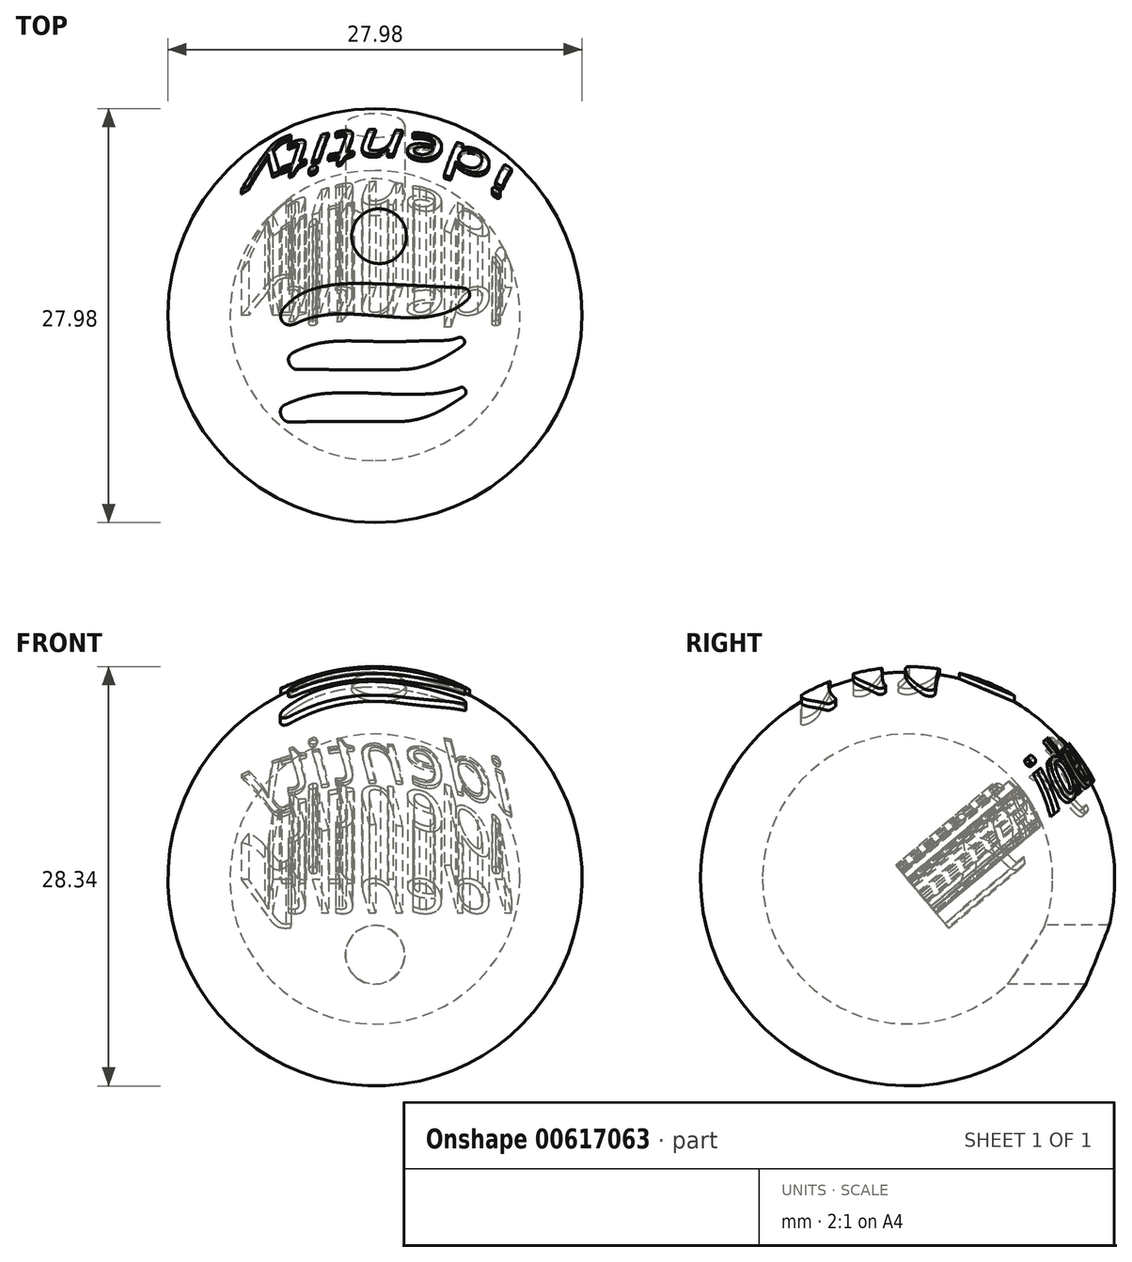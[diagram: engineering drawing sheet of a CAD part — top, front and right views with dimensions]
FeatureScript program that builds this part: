
annotation { "Feature Type Name" : "Feature", "Feature Type Description" : "" }
export const myFeature = defineFeature(function(context is Context, id is Id, definition is map)
    precondition{}
    {
        {
            var Q0;
            Q0=qCreatedBy(makeId("Top.planeOp"),FACE);
            var sketch = newSketch(context, id + "F0", { "sketchPlane" : qUnion([Q0])});
            skLineSegment(sketch, "E0", {"start": v(0, -10) * mm, "end": v(0, 10) * mm});
            skArc(sketch, "E1", {"start": v(0, 10) * mm, "mid": v(-10, 0) * mm, "end": v(0, -10) * mm});
            skSolve(sketch);
        }
        {
            var Q0;
            {var subQ0=sQuery(id+"F0.wireOp",EDGE,"E1");Q0=makeQuery(id+"F0.imprint","IMPRINT",FACE,{"disambiguationData":[TD([[makeQuery(id+"F0.imprint","IMPRINT",EDGE,{"derivedFrom":subQ0}),1.0]])]});}
            var Q1;
            Q1=sQuery(id+"F0.wireOp",EDGE,"E0");
            revolve(context, id + "F1", {"entities" : qUnion([Q0]), "axis" : qUnion([Q1]), "revolveType" : RevolveType.FULL});
        }
        {
            var Q0;
            Q0=makeQuery(id+"F1.opRevolve","SWEPT_BODY",BODY,{"disambiguationData":[OSD([sQuery(id+"F0.wireOp",EDGE,"E0"),sQuery(id+"F0.wireOp",EDGE,"E1")])]});
            var Q1;
            Q1=sQuery(id+"F0.wireOp",VERTEX,"NPe4G0ez-t7S9-9isL-QO5v-uuJu600mHcIT.center");
            var Q2;
            Q2=sQuery(id+"F0.wireOp",VERTEX,"E1.center");
            transform(context, id + "F2", {"entities" : qUnion([Q0]), "transformType" : TransformType.SCALE_UNIFORMLY, "scale" : 33.3, "scalePoint" : qUnion([Q2]), "makeCopy" : false});
        }
        {
            var Q0;
            Q0=qCreatedBy(makeId("Top.planeOp"),FACE);
            var sketch = newSketch(context, id + "F3", { "sketchPlane" : qUnion([Q0])});
            skArc(sketch, "E2", {"start": v(-4.66, 170.28) * mm, "mid": v(-7.58, 169.39) * mm, "end": v(-10.43, 168.3) * mm});
            skArc(sketch, "E3", {"start": v(-10.43, 168.3) * mm, "mid": v(-13.1, 167.06) * mm, "end": v(-15.68, 165.63) * mm});
            skArc(sketch, "E4", {"start": v(-15.68, 165.63) * mm, "mid": v(-18.2, 163.97) * mm, "end": v(-20.58, 162.14) * mm});
            skArc(sketch, "E5", {"start": v(-20.58, 162.14) * mm, "mid": v(-23, 160) * mm, "end": v(-25.3, 157.73) * mm});
            skArc(sketch, "E6", {"start": v(-25.3, 157.73) * mm, "mid": v(-31.47, 149.54) * mm, "end": v(-35.58, 140.15) * mm});
            skArc(sketch, "E7", {"start": v(-35.58, 140.15) * mm, "mid": v(-37.42, 130.07) * mm, "end": v(-36.87, 119.84) * mm});
            skArc(sketch, "E8", {"start": v(-36.87, 119.84) * mm, "mid": v(-33.98, 110.06) * mm, "end": v(-28.9, 101.23) * mm});
            skArc(sketch, "E9", {"start": v(-28.9, 101.23) * mm, "mid": v(-21.93, 93.88) * mm, "end": v(-13.42, 88.39) * mm});
            skArc(sketch, "E10", {"start": v(-13.42, 88.39) * mm, "mid": v(-4.52, 85.1) * mm, "end": v(4.86, 83.64) * mm});
            skArc(sketch, "E11", {"start": v(4.86, 83.64) * mm, "mid": v(14.1, 84.14) * mm, "end": v(23, 86.6) * mm});
            skArc(sketch, "E12", {"start": v(23, 86.6) * mm, "mid": v(31.14, 90.88) * mm, "end": v(38.15, 96.82) * mm});
            skArc(sketch, "E13", {"start": v(38.15, 96.82) * mm, "mid": v(43.87, 104.23) * mm, "end": v(47.95, 112.66) * mm});
            skArc(sketch, "E14", {"start": v(47.95, 112.66) * mm, "mid": v(48.9, 115.67) * mm, "end": v(49.58, 118.75) * mm});
            skArc(sketch, "E15", {"start": v(49.58, 118.75) * mm, "mid": v(50.08, 122.26) * mm, "end": v(50.36, 125.8) * mm});
            skArc(sketch, "E16", {"start": v(50.36, 125.8) * mm, "mid": v(50.43, 129.3) * mm, "end": v(50.27, 132.82) * mm});
            skArc(sketch, "E17", {"start": v(50.27, 132.82) * mm, "mid": v(49.9, 135.86) * mm, "end": v(49.24, 138.85) * mm});
            skArc(sketch, "E18", {"start": v(49.24, 138.85) * mm, "mid": v(46.19, 146.9) * mm, "end": v(41.61, 154.2) * mm});
            skArc(sketch, "E19", {"start": v(41.61, 154.2) * mm, "mid": v(35.64, 160.54) * mm, "end": v(28.58, 165.62) * mm});
            skArc(sketch, "E20", {"start": v(28.58, 165.62) * mm, "mid": v(20.7, 169.25) * mm, "end": v(12.28, 171.3) * mm});
            skArc(sketch, "E21", {"start": v(12.28, 171.3) * mm, "mid": v(3.76, 171.65) * mm, "end": v(-4.66, 170.28) * mm});
            skArc(sketch, "E22", {"start": v(-53.26, 50.77) * mm, "mid": v(-64.06, 49.8) * mm, "end": v(-74.8, 48.33) * mm});
            skArc(sketch, "E23", {"start": v(-74.8, 48.33) * mm, "mid": v(-84.6, 46.48) * mm, "end": v(-94.27, 44.06) * mm});
            skArc(sketch, "E24", {"start": v(-94.27, 44.06) * mm, "mid": v(-102.95, 41.3) * mm, "end": v(-111.44, 38.01) * mm});
            skArc(sketch, "E25", {"start": v(-111.44, 38.01) * mm, "mid": v(-118.91, 34.44) * mm, "end": v(-126.06, 30.25) * mm});
            skArc(sketch, "E26", {"start": v(-126.06, 30.25) * mm, "mid": v(-129.48, 27.88) * mm, "end": v(-132.74, 25.3) * mm});
            skArc(sketch, "E27", {"start": v(-132.74, 25.3) * mm, "mid": v(-136.56, 21.93) * mm, "end": v(-140.26, 18.43) * mm});
            skArc(sketch, "E28", {"start": v(-140.26, 18.43) * mm, "mid": v(-143.63, 15) * mm, "end": v(-146.88, 11.47) * mm});
            skArc(sketch, "E29", {"start": v(-146.88, 11.47) * mm, "mid": v(-148.63, 9.2) * mm, "end": v(-150.04, 6.7) * mm});
            skArc(sketch, "E30", {"start": v(-150.04, 6.7) * mm, "mid": v(-151.12, 3.79) * mm, "end": v(-151.7, 0.72) * mm});
            skArc(sketch, "E31", {"start": v(-151.7, 0.72) * mm, "mid": v(-151.7, -2.28) * mm, "end": v(-151.14, -5.22) * mm});
            skArc(sketch, "E32", {"start": v(-151.14, -5.22) * mm, "mid": v(-150.05, -7.88) * mm, "end": v(-148.44, -10.26) * mm});
            skArc(sketch, "E33", {"start": v(-148.44, -10.26) * mm, "mid": v(-146.42, -12.22) * mm, "end": v(-144.02, -13.69) * mm});
            skArc(sketch, "E34", {"start": v(-144.02, -13.69) * mm, "mid": v(-142.01, -14.5) * mm, "end": v(-139.92, -15.03) * mm});
            skArc(sketch, "E35", {"start": v(-139.92, -15.03) * mm, "mid": v(-137.8, -15.3) * mm, "end": v(-135.66, -15.27) * mm});
            skArc(sketch, "E36", {"start": v(-135.66, -15.27) * mm, "mid": v(-133.36, -14.96) * mm, "end": v(-131.12, -14.38) * mm});
            skArc(sketch, "E37", {"start": v(-131.12, -14.38) * mm, "mid": v(-128.6, -13.46) * mm, "end": v(-126.17, -12.35) * mm});
            skArc(sketch, "E38", {"start": v(-126.17, -12.35) * mm, "mid": v(-117.46, -8.41) * mm, "end": v(-108.44, -5.24) * mm});
            skArc(sketch, "E39", {"start": v(-108.44, -5.24) * mm, "mid": v(-98.18, -2.46) * mm, "end": v(-87.78, -0.33) * mm});
            skArc(sketch, "E40", {"start": v(-87.78, -0.33) * mm, "mid": v(-76.35, 1.3) * mm, "end": v(-64.84, 2.26) * mm});
            skArc(sketch, "E41", {"start": v(-64.84, 2.26) * mm, "mid": v(-52.55, 2.64) * mm, "end": v(-40.26, 2.43) * mm});
            skArc(sketch, "E42", {"start": v(-40.26, 2.43) * mm, "mid": v(-36.4, 2.26) * mm, "end": v(-32.52, 2.05) * mm});
            skArc(sketch, "E43", {"start": v(-32.52, 2.05) * mm, "mid": v(-27.36, 1.73) * mm, "end": v(-22.2, 1.4) * mm});
            skArc(sketch, "E44", {"start": v(-22.2, 1.4) * mm, "mid": v(-16.72, 1.02) * mm, "end": v(-11.24, 0.63) * mm});
            skArc(sketch, "E45", {"start": v(-11.24, 0.63) * mm, "mid": v(-6.25, 0.24) * mm, "end": v(-1.26, -0.16) * mm});
            skArc(sketch, "E46", {"start": v(-1.26, -0.16) * mm, "mid": v(3.81, -0.58) * mm, "end": v(8.89, -0.98) * mm});
            skArc(sketch, "E47", {"start": v(8.89, -0.98) * mm, "mid": v(14.64, -1.41) * mm, "end": v(20.4, -1.83) * mm});
            skArc(sketch, "E48", {"start": v(20.4, -1.83) * mm, "mid": v(25.93, -2.22) * mm, "end": v(31.47, -2.59) * mm});
            skArc(sketch, "E49", {"start": v(31.47, -2.59) * mm, "mid": v(35.82, -2.86) * mm, "end": v(40.17, -3.11) * mm});
            skArc(sketch, "E50", {"start": v(40.17, -3.11) * mm, "mid": v(56.95, -3.55) * mm, "end": v(73.73, -3.04) * mm});
            skArc(sketch, "E51", {"start": v(73.73, -3.04) * mm, "mid": v(87.98, -1.56) * mm, "end": v(102.05, 1.2) * mm});
            skArc(sketch, "E52", {"start": v(102.05, 1.2) * mm, "mid": v(114.17, 4.83) * mm, "end": v(125.84, 9.71) * mm});
            skArc(sketch, "E53", {"start": v(125.84, 9.71) * mm, "mid": v(136.2, 15.52) * mm, "end": v(145.73, 22.6) * mm});
            skArc(sketch, "E54", {"start": v(145.73, 22.6) * mm, "mid": v(146.55, 23.31) * mm, "end": v(147.35, 24.05) * mm});
            skArc(sketch, "E55", {"start": v(147.35, 24.05) * mm, "mid": v(148.14, 24.82) * mm, "end": v(148.9, 25.62) * mm});
            skArc(sketch, "E56", {"start": v(148.9, 25.62) * mm, "mid": v(149.57, 26.35) * mm, "end": v(150.21, 27.1) * mm});
            skArc(sketch, "E57", {"start": v(150.21, 27.1) * mm, "mid": v(150.6, 27.61) * mm, "end": v(150.94, 28.16) * mm});
            skArc(sketch, "E58", {"start": v(150.94, 28.16) * mm, "mid": v(151.52, 29.44) * mm, "end": v(151.89, 30.8) * mm});
            skArc(sketch, "E59", {"start": v(151.89, 30.8) * mm, "mid": v(152.1, 32.43) * mm, "end": v(152.15, 34.07) * mm});
            skArc(sketch, "E60", {"start": v(152.15, 34.07) * mm, "mid": v(152.02, 35.68) * mm, "end": v(151.74, 37.26) * mm});
            skArc(sketch, "E61", {"start": v(151.74, 37.26) * mm, "mid": v(151.32, 38.5) * mm, "end": v(150.68, 39.64) * mm});
            skArc(sketch, "E62", {"start": v(150.68, 39.64) * mm, "mid": v(149.45, 41.07) * mm, "end": v(147.96, 42.23) * mm});
            skArc(sketch, "E63", {"start": v(147.96, 42.23) * mm, "mid": v(146.18, 43.15) * mm, "end": v(144.28, 43.77) * mm});
            skArc(sketch, "E64", {"start": v(144.28, 43.77) * mm, "mid": v(141.31, 44.35) * mm, "end": v(138.3, 44.68) * mm});
            skArc(sketch, "E65", {"start": v(138.3, 44.68) * mm, "mid": v(132.52, 45.03) * mm, "end": v(126.74, 45.3) * mm});
            skArc(sketch, "E66", {"start": v(126.74, 45.3) * mm, "mid": v(122.24, 45.48) * mm, "end": v(117.75, 45.68) * mm});
            skArc(sketch, "E67", {"start": v(117.75, 45.68) * mm, "mid": v(110.73, 46) * mm, "end": v(103.71, 46.34) * mm});
            skArc(sketch, "E68", {"start": v(103.71, 46.34) * mm, "mid": v(95.78, 46.73) * mm, "end": v(87.84, 47.12) * mm});
            skArc(sketch, "E69", {"start": v(87.84, 47.12) * mm, "mid": v(80.04, 47.51) * mm, "end": v(72.24, 47.91) * mm});
            skArc(sketch, "E70", {"start": v(72.24, 47.91) * mm, "mid": v(47.98, 49.13) * mm, "end": v(23.71, 50.25) * mm});
            skArc(sketch, "E71", {"start": v(23.71, 50.25) * mm, "mid": v(7.3, 50.9) * mm, "end": v(-9.1, 51.36) * mm});
            skArc(sketch, "E72", {"start": v(-9.1, 51.36) * mm, "mid": v(-21.25, 51.54) * mm, "end": v(-33.4, 51.52) * mm});
            skArc(sketch, "E73", {"start": v(-33.4, 51.52) * mm, "mid": v(-43.34, 51.29) * mm, "end": v(-53.26, 50.77) * mm});
            skArc(sketch, "E74", {"start": v(132.24, -36.27) * mm, "mid": v(128.84, -37.48) * mm, "end": v(125.36, -38.43) * mm});
            skArc(sketch, "E75", {"start": v(125.36, -38.43) * mm, "mid": v(121.58, -39.19) * mm, "end": v(117.76, -39.7) * mm});
            skArc(sketch, "E76", {"start": v(117.76, -39.7) * mm, "mid": v(112.5, -40.14) * mm, "end": v(107.22, -40.38) * mm});
            skArc(sketch, "E77", {"start": v(107.22, -40.38) * mm, "mid": v(98.48, -40.56) * mm, "end": v(89.74, -40.66) * mm});
            skArc(sketch, "E78", {"start": v(89.74, -40.66) * mm, "mid": v(84.02, -40.72) * mm, "end": v(78.3, -40.8) * mm});
            skArc(sketch, "E79", {"start": v(78.3, -40.8) * mm, "mid": v(72.28, -40.94) * mm, "end": v(66.26, -41.1) * mm});
            skArc(sketch, "E80", {"start": v(66.26, -41.1) * mm, "mid": v(60.8, -41.28) * mm, "end": v(55.33, -41.48) * mm});
            skArc(sketch, "E81", {"start": v(55.33, -41.48) * mm, "mid": v(51.53, -41.66) * mm, "end": v(47.74, -41.9) * mm});
            skArc(sketch, "E82", {"start": v(47.74, -41.9) * mm, "mid": v(43.15, -42.17) * mm, "end": v(38.56, -42.33) * mm});
            skArc(sketch, "E83", {"start": v(38.56, -42.33) * mm, "mid": v(33.12, -42.42) * mm, "end": v(27.68, -42.43) * mm});
            skArc(sketch, "E84", {"start": v(27.68, -42.43) * mm, "mid": v(20.74, -42.36) * mm, "end": v(13.8, -42.21) * mm});
            skArc(sketch, "E85", {"start": v(13.8, -42.21) * mm, "mid": v(4.36, -41.94) * mm, "end": v(-5.07, -41.63) * mm});
            skArc(sketch, "E86", {"start": v(-5.07, -41.63) * mm, "mid": v(-26.65, -41.09) * mm, "end": v(-48.23, -40.97) * mm});
            skArc(sketch, "E87", {"start": v(-48.23, -40.97) * mm, "mid": v(-63.07, -41.48) * mm, "end": v(-77.86, -42.86) * mm});
            skArc(sketch, "E88", {"start": v(-77.86, -42.86) * mm, "mid": v(-89.81, -44.81) * mm, "end": v(-101.57, -47.7) * mm});
            skArc(sketch, "E89", {"start": v(-101.57, -47.7) * mm, "mid": v(-113.32, -51.59) * mm, "end": v(-124.74, -56.33) * mm});
            skArc(sketch, "E90", {"start": v(-124.74, -56.33) * mm, "mid": v(-127.9, -57.83) * mm, "end": v(-131.02, -59.43) * mm});
            skArc(sketch, "E91", {"start": v(-131.02, -59.43) * mm, "mid": v(-132.98, -60.6) * mm, "end": v(-134.82, -61.95) * mm});
            skArc(sketch, "E92", {"start": v(-134.82, -61.95) * mm, "mid": v(-136.11, -63.16) * mm, "end": v(-137.22, -64.54) * mm});
            skArc(sketch, "E93", {"start": v(-137.22, -64.54) * mm, "mid": v(-138.12, -66.08) * mm, "end": v(-138.8, -67.72) * mm});
            skArc(sketch, "E94", {"start": v(-138.8, -67.72) * mm, "mid": v(-139.28, -70.2) * mm, "end": v(-139.15, -72.73) * mm});
            skArc(sketch, "E95", {"start": v(-139.15, -72.73) * mm, "mid": v(-138.4, -75.61) * mm, "end": v(-137.23, -78.35) * mm});
            skArc(sketch, "E96", {"start": v(-137.23, -78.35) * mm, "mid": v(-135.62, -80.94) * mm, "end": v(-133.64, -83.26) * mm});
            skArc(sketch, "E97", {"start": v(-133.64, -83.26) * mm, "mid": v(-131.55, -84.96) * mm, "end": v(-129.14, -86.19) * mm});
            skArc(sketch, "E98", {"start": v(-129.14, -86.19) * mm, "mid": v(-128.26, -86.44) * mm, "end": v(-127.36, -86.53) * mm});
            skArc(sketch, "E99", {"start": v(-127.36, -86.53) * mm, "mid": v(-114.43, -86.69) * mm, "end": v(-101.5, -86.84) * mm});
            skArc(sketch, "E100", {"start": v(-101.5, -86.84) * mm, "mid": v(-86.92, -86.99) * mm, "end": v(-72.34, -87.1) * mm});
            skArc(sketch, "E101", {"start": v(-72.34, -87.1) * mm, "mid": v(-55.23, -87.19) * mm, "end": v(-38.12, -87.25) * mm});
            skArc(sketch, "E102", {"start": v(-38.12, -87.25) * mm, "mid": v(-5.06, -87.3) * mm, "end": v(28, -87.3) * mm});
            skArc(sketch, "E103", {"start": v(28, -87.3) * mm, "mid": v(39.54, -87.11) * mm, "end": v(51.07, -86.6) * mm});
            skArc(sketch, "E104", {"start": v(51.07, -86.6) * mm, "mid": v(58.6, -85.87) * mm, "end": v(66.04, -84.57) * mm});
            skArc(sketch, "E105", {"start": v(66.04, -84.57) * mm, "mid": v(74.26, -82.58) * mm, "end": v(82.35, -80.14) * mm});
            skArc(sketch, "E106", {"start": v(82.35, -80.14) * mm, "mid": v(88.6, -77.93) * mm, "end": v(94.73, -75.44) * mm});
            skArc(sketch, "E107", {"start": v(94.73, -75.44) * mm, "mid": v(101.06, -72.56) * mm, "end": v(107.27, -69.46) * mm});
            skArc(sketch, "E108", {"start": v(107.27, -69.46) * mm, "mid": v(114.04, -65.76) * mm, "end": v(120.68, -61.83) * mm});
            skArc(sketch, "E109", {"start": v(120.68, -61.83) * mm, "mid": v(128.26, -57.07) * mm, "end": v(135.74, -52.14) * mm});
            skArc(sketch, "E110", {"start": v(135.74, -52.14) * mm, "mid": v(138.65, -50.07) * mm, "end": v(141.45, -47.85) * mm});
            skArc(sketch, "E111", {"start": v(141.45, -47.85) * mm, "mid": v(142.88, -46.36) * mm, "end": v(143.94, -44.58) * mm});
            skArc(sketch, "E112", {"start": v(143.94, -44.58) * mm, "mid": v(144.31, -43.02) * mm, "end": v(144.1, -41.42) * mm});
            skArc(sketch, "E113", {"start": v(144.1, -41.42) * mm, "mid": v(143.3, -39.51) * mm, "end": v(142.16, -37.78) * mm});
            skArc(sketch, "E114", {"start": v(142.16, -37.78) * mm, "mid": v(141.3, -36.86) * mm, "end": v(140.3, -36.12) * mm});
            skArc(sketch, "E115", {"start": v(140.3, -36.12) * mm, "mid": v(139.22, -35.6) * mm, "end": v(138.05, -35.3) * mm});
            skArc(sketch, "E116", {"start": v(138.05, -35.3) * mm, "mid": v(136.7, -35.2) * mm, "end": v(135.37, -35.35) * mm});
            skArc(sketch, "E117", {"start": v(135.37, -35.35) * mm, "mid": v(133.78, -35.73) * mm, "end": v(132.24, -36.27) * mm});
            skArc(sketch, "E118", {"start": v(135.24, -116.75) * mm, "mid": v(132.5, -117.85) * mm, "end": v(129.68, -118.77) * mm});
            skArc(sketch, "E119", {"start": v(129.68, -118.77) * mm, "mid": v(125.46, -119.96) * mm, "end": v(121.21, -121.05) * mm});
            skArc(sketch, "E120", {"start": v(121.21, -121.05) * mm, "mid": v(116.55, -122.15) * mm, "end": v(111.87, -123.15) * mm});
            skArc(sketch, "E121", {"start": v(111.87, -123.15) * mm, "mid": v(107.55, -123.97) * mm, "end": v(103.2, -124.67) * mm});
            skArc(sketch, "E122", {"start": v(103.2, -124.67) * mm, "mid": v(96.18, -125.52) * mm, "end": v(89.12, -126.04) * mm});
            skArc(sketch, "E123", {"start": v(89.12, -126.04) * mm, "mid": v(78.35, -126.48) * mm, "end": v(67.57, -126.77) * mm});
            skArc(sketch, "E124", {"start": v(67.57, -126.77) * mm, "mid": v(55.76, -126.9) * mm, "end": v(43.96, -126.87) * mm});
            skArc(sketch, "E125", {"start": v(43.96, -126.87) * mm, "mid": v(33.1, -126.66) * mm, "end": v(22.24, -126.23) * mm});
            skArc(sketch, "E126", {"start": v(22.24, -126.23) * mm, "mid": v(0.62, -125.28) * mm, "end": v(-21.01, -124.56) * mm});
            skArc(sketch, "E127", {"start": v(-21.01, -124.56) * mm, "mid": v(-37.49, -124.27) * mm, "end": v(-53.97, -124.36) * mm});
            skArc(sketch, "E128", {"start": v(-53.97, -124.36) * mm, "mid": v(-66.78, -124.76) * mm, "end": v(-79.57, -125.53) * mm});
            skArc(sketch, "E129", {"start": v(-79.57, -125.53) * mm, "mid": v(-89.46, -126.58) * mm, "end": v(-99.26, -128.24) * mm});
            skArc(sketch, "E130", {"start": v(-99.26, -128.24) * mm, "mid": v(-106.51, -129.88) * mm, "end": v(-113.67, -131.89) * mm});
            skArc(sketch, "E131", {"start": v(-113.67, -131.89) * mm, "mid": v(-121.75, -134.52) * mm, "end": v(-129.74, -137.41) * mm});
            skArc(sketch, "E132", {"start": v(-129.74, -137.41) * mm, "mid": v(-137, -140.3) * mm, "end": v(-144.2, -143.36) * mm});
            skArc(sketch, "E133", {"start": v(-144.2, -143.36) * mm, "mid": v(-147.14, -145.1) * mm, "end": v(-149.61, -147.46) * mm});
            skArc(sketch, "E134", {"start": v(-149.61, -147.46) * mm, "mid": v(-150.87, -149.37) * mm, "end": v(-151.68, -151.5) * mm});
            skArc(sketch, "E135", {"start": v(-151.68, -151.5) * mm, "mid": v(-152.1, -153.97) * mm, "end": v(-152.1, -156.48) * mm});
            skArc(sketch, "E136", {"start": v(-152.1, -156.48) * mm, "mid": v(-151.67, -159.11) * mm, "end": v(-150.83, -161.64) * mm});
            skArc(sketch, "E137", {"start": v(-150.83, -161.64) * mm, "mid": v(-149.6, -164.04) * mm, "end": v(-148.03, -166.23) * mm});
            skArc(sketch, "E138", {"start": v(-148.03, -166.23) * mm, "mid": v(-146.16, -168.12) * mm, "end": v(-143.99, -169.67) * mm});
            skArc(sketch, "E139", {"start": v(-143.99, -169.67) * mm, "mid": v(-141.73, -170.72) * mm, "end": v(-139.3, -171.3) * mm});
            skArc(sketch, "E140", {"start": v(-139.3, -171.3) * mm, "mid": v(-135.4, -171.66) * mm, "end": v(-131.46, -171.7) * mm});
            skArc(sketch, "E141", {"start": v(-131.46, -171.7) * mm, "mid": v(-121.5, -171.4) * mm, "end": v(-111.54, -171.03) * mm});
            skArc(sketch, "E142", {"start": v(-111.54, -171.03) * mm, "mid": v(-103.76, -170.76) * mm, "end": v(-95.98, -170.6) * mm});
            skArc(sketch, "E143", {"start": v(-95.98, -170.6) * mm, "mid": v(-85.5, -170.46) * mm, "end": v(-75.03, -170.38) * mm});
            skArc(sketch, "E144", {"start": v(-75.03, -170.38) * mm, "mid": v(-62.49, -170.34) * mm, "end": v(-49.94, -170.37) * mm});
            skArc(sketch, "E145", {"start": v(-49.94, -170.37) * mm, "mid": v(-35.6, -170.45) * mm, "end": v(-21.26, -170.57) * mm});
            skArc(sketch, "E146", {"start": v(-21.26, -170.57) * mm, "mid": v(-4, -170.74) * mm, "end": v(13.28, -170.87) * mm});
            skArc(sketch, "E147", {"start": v(13.28, -170.87) * mm, "mid": v(22.74, -170.9) * mm, "end": v(32.2, -170.83) * mm});
            skArc(sketch, "E148", {"start": v(32.2, -170.83) * mm, "mid": v(38.3, -170.7) * mm, "end": v(44.39, -170.49) * mm});
            skArc(sketch, "E149", {"start": v(44.39, -170.49) * mm, "mid": v(48.72, -170.2) * mm, "end": v(53.04, -169.72) * mm});
            skArc(sketch, "E150", {"start": v(53.04, -169.72) * mm, "mid": v(59.66, -168.72) * mm, "end": v(66.24, -167.45) * mm});
            skArc(sketch, "E151", {"start": v(66.24, -167.45) * mm, "mid": v(72.42, -166) * mm, "end": v(78.53, -164.27) * mm});
            skArc(sketch, "E152", {"start": v(78.53, -164.27) * mm, "mid": v(84.55, -162.26) * mm, "end": v(90.47, -159.99) * mm});
            skArc(sketch, "E153", {"start": v(90.47, -159.99) * mm, "mid": v(96.6, -157.34) * mm, "end": v(102.62, -154.45) * mm});
            skArc(sketch, "E154", {"start": v(102.62, -154.45) * mm, "mid": v(108.05, -151.59) * mm, "end": v(113.38, -148.53) * mm});
            skArc(sketch, "E155", {"start": v(113.38, -148.53) * mm, "mid": v(120.4, -144.25) * mm, "end": v(127.35, -139.87) * mm});
            skArc(sketch, "E156", {"start": v(127.35, -139.87) * mm, "mid": v(134.12, -135.48) * mm, "end": v(140.85, -131.03) * mm});
            skArc(sketch, "E157", {"start": v(140.85, -131.03) * mm, "mid": v(143.06, -129.3) * mm, "end": v(144.99, -127.28) * mm});
            skArc(sketch, "E158", {"start": v(144.99, -127.28) * mm, "mid": v(145.63, -126.28) * mm, "end": v(146.03, -125.15) * mm});
            skArc(sketch, "E159", {"start": v(146.03, -125.15) * mm, "mid": v(146.2, -123.84) * mm, "end": v(146.15, -122.51) * mm});
            skArc(sketch, "E160", {"start": v(146.15, -122.51) * mm, "mid": v(145.87, -121.14) * mm, "end": v(145.37, -119.84) * mm});
            skArc(sketch, "E161", {"start": v(145.37, -119.84) * mm, "mid": v(144.67, -118.65) * mm, "end": v(143.78, -117.6) * mm});
            skArc(sketch, "E162", {"start": v(143.78, -117.6) * mm, "mid": v(142.83, -116.72) * mm, "end": v(141.82, -115.92) * mm});
            skArc(sketch, "E163", {"start": v(141.82, -115.92) * mm, "mid": v(141.06, -115.52) * mm, "end": v(140.23, -115.33) * mm});
            skArc(sketch, "E164", {"start": v(140.23, -115.33) * mm, "mid": v(139.29, -115.33) * mm, "end": v(138.36, -115.54) * mm});
            skArc(sketch, "E165", {"start": v(138.36, -115.54) * mm, "mid": v(136.79, -116.11) * mm, "end": v(135.24, -116.75) * mm});
            skSolve(sketch);
        }
        {
            var Q0;
            Q0=qSketchRegion(id+"F3",true);
            var Q1;
            Q1=sQuery(id+"F3.wireOp",EDGE,"E25");
            var Q2;
            Q2=sQuery(id+"F3.wireOp",EDGE,"E24");
            extrude(context, id + "F4", {"entities" : qUnion([Q0]), "operationType" : NewBodyOperationType.ADD, "surfaceEntities" : qUnion([Q1, Q2]), "depth" : 350 * mm});
        }
        {
            var Q0;
            Q0=makeQuery(id+"F4.opExtrude","SWEPT_BODY",BODY,{"disambiguationData":[OSD([sQuery(id+"F3.wireOp",EDGE,"E74"),sQuery(id+"F3.wireOp",EDGE,"E75"),sQuery(id+"F3.wireOp",EDGE,"E76"),sQuery(id+"F3.wireOp",EDGE,"E77"),sQuery(id+"F3.wireOp",EDGE,"E78"),sQuery(id+"F3.wireOp",EDGE,"E79"),sQuery(id+"F3.wireOp",EDGE,"E80"),sQuery(id+"F3.wireOp",EDGE,"E81"),sQuery(id+"F3.wireOp",EDGE,"E82"),sQuery(id+"F3.wireOp",EDGE,"E83"),sQuery(id+"F3.wireOp",EDGE,"E84"),sQuery(id+"F3.wireOp",EDGE,"E85"),sQuery(id+"F3.wireOp",EDGE,"E86"),sQuery(id+"F3.wireOp",EDGE,"E87"),sQuery(id+"F3.wireOp",EDGE,"E88"),sQuery(id+"F3.wireOp",EDGE,"E89"),sQuery(id+"F3.wireOp",EDGE,"E90"),sQuery(id+"F3.wireOp",EDGE,"E91"),sQuery(id+"F3.wireOp",EDGE,"E92"),sQuery(id+"F3.wireOp",EDGE,"E93"),sQuery(id+"F3.wireOp",EDGE,"E94"),sQuery(id+"F3.wireOp",EDGE,"E95"),sQuery(id+"F3.wireOp",EDGE,"E96"),sQuery(id+"F3.wireOp",EDGE,"E97"),sQuery(id+"F3.wireOp",EDGE,"E98"),sQuery(id+"F3.wireOp",EDGE,"E99"),sQuery(id+"F3.wireOp",EDGE,"E100"),sQuery(id+"F3.wireOp",EDGE,"E101"),sQuery(id+"F3.wireOp",EDGE,"E102"),sQuery(id+"F3.wireOp",EDGE,"E103"),sQuery(id+"F3.wireOp",EDGE,"E104"),sQuery(id+"F3.wireOp",EDGE,"E105"),sQuery(id+"F3.wireOp",EDGE,"E106"),sQuery(id+"F3.wireOp",EDGE,"E107"),sQuery(id+"F3.wireOp",EDGE,"E108"),sQuery(id+"F3.wireOp",EDGE,"E109"),sQuery(id+"F3.wireOp",EDGE,"E110"),sQuery(id+"F3.wireOp",EDGE,"E111"),sQuery(id+"F3.wireOp",EDGE,"E112"),sQuery(id+"F3.wireOp",EDGE,"E113"),sQuery(id+"F3.wireOp",EDGE,"E114"),sQuery(id+"F3.wireOp",EDGE,"E115"),sQuery(id+"F3.wireOp",EDGE,"E116"),sQuery(id+"F3.wireOp",EDGE,"E117")])]});
            var Q1;
            Q1=makeQuery(id+"F4.opExtrude","SWEPT_BODY",BODY,{"disambiguationData":[OSD([sQuery(id+"F3.wireOp",EDGE,"E118"),sQuery(id+"F3.wireOp",EDGE,"E119"),sQuery(id+"F3.wireOp",EDGE,"E120"),sQuery(id+"F3.wireOp",EDGE,"E121"),sQuery(id+"F3.wireOp",EDGE,"E122"),sQuery(id+"F3.wireOp",EDGE,"E123"),sQuery(id+"F3.wireOp",EDGE,"E124"),sQuery(id+"F3.wireOp",EDGE,"E125"),sQuery(id+"F3.wireOp",EDGE,"E126"),sQuery(id+"F3.wireOp",EDGE,"E127"),sQuery(id+"F3.wireOp",EDGE,"E128"),sQuery(id+"F3.wireOp",EDGE,"E129"),sQuery(id+"F3.wireOp",EDGE,"E130"),sQuery(id+"F3.wireOp",EDGE,"E131"),sQuery(id+"F3.wireOp",EDGE,"E132"),sQuery(id+"F3.wireOp",EDGE,"E133"),sQuery(id+"F3.wireOp",EDGE,"E134"),sQuery(id+"F3.wireOp",EDGE,"E135"),sQuery(id+"F3.wireOp",EDGE,"E136"),sQuery(id+"F3.wireOp",EDGE,"E137"),sQuery(id+"F3.wireOp",EDGE,"E138"),sQuery(id+"F3.wireOp",EDGE,"E139"),sQuery(id+"F3.wireOp",EDGE,"E140"),sQuery(id+"F3.wireOp",EDGE,"E141"),sQuery(id+"F3.wireOp",EDGE,"E142"),sQuery(id+"F3.wireOp",EDGE,"E143"),sQuery(id+"F3.wireOp",EDGE,"E144"),sQuery(id+"F3.wireOp",EDGE,"E145"),sQuery(id+"F3.wireOp",EDGE,"E146"),sQuery(id+"F3.wireOp",EDGE,"E147"),sQuery(id+"F3.wireOp",EDGE,"E148"),sQuery(id+"F3.wireOp",EDGE,"E149"),sQuery(id+"F3.wireOp",EDGE,"E150"),sQuery(id+"F3.wireOp",EDGE,"E151"),sQuery(id+"F3.wireOp",EDGE,"E152"),sQuery(id+"F3.wireOp",EDGE,"E153"),sQuery(id+"F3.wireOp",EDGE,"E154"),sQuery(id+"F3.wireOp",EDGE,"E155"),sQuery(id+"F3.wireOp",EDGE,"E156"),sQuery(id+"F3.wireOp",EDGE,"E157"),sQuery(id+"F3.wireOp",EDGE,"E158"),sQuery(id+"F3.wireOp",EDGE,"E159"),sQuery(id+"F3.wireOp",EDGE,"E160"),sQuery(id+"F3.wireOp",EDGE,"E161"),sQuery(id+"F3.wireOp",EDGE,"E162"),sQuery(id+"F3.wireOp",EDGE,"E163"),sQuery(id+"F3.wireOp",EDGE,"E164"),sQuery(id+"F3.wireOp",EDGE,"E165")])]});
            var Q2;
            Q2=makeQuery(id+"F4.opExtrude","SWEPT_BODY",BODY,{"disambiguationData":[OSD([sQuery(id+"F3.wireOp",EDGE,"E2"),sQuery(id+"F3.wireOp",EDGE,"E3"),sQuery(id+"F3.wireOp",EDGE,"E4"),sQuery(id+"F3.wireOp",EDGE,"E5"),sQuery(id+"F3.wireOp",EDGE,"E6"),sQuery(id+"F3.wireOp",EDGE,"E7"),sQuery(id+"F3.wireOp",EDGE,"E8"),sQuery(id+"F3.wireOp",EDGE,"E9"),sQuery(id+"F3.wireOp",EDGE,"E10"),sQuery(id+"F3.wireOp",EDGE,"E11"),sQuery(id+"F3.wireOp",EDGE,"E12"),sQuery(id+"F3.wireOp",EDGE,"E13"),sQuery(id+"F3.wireOp",EDGE,"E14"),sQuery(id+"F3.wireOp",EDGE,"E15"),sQuery(id+"F3.wireOp",EDGE,"E16"),sQuery(id+"F3.wireOp",EDGE,"E17"),sQuery(id+"F3.wireOp",EDGE,"E18"),sQuery(id+"F3.wireOp",EDGE,"E19"),sQuery(id+"F3.wireOp",EDGE,"E20"),sQuery(id+"F3.wireOp",EDGE,"E21")])]});
            var Q3;
            Q3=makeQuery(id+"F4.opExtrude","SWEPT_BODY",BODY,{"disambiguationData":[OSD([sQuery(id+"F3.wireOp",EDGE,"E22"),sQuery(id+"F3.wireOp",EDGE,"E23"),sQuery(id+"F3.wireOp",EDGE,"E24"),sQuery(id+"F3.wireOp",EDGE,"E25"),sQuery(id+"F3.wireOp",EDGE,"E26"),sQuery(id+"F3.wireOp",EDGE,"E27"),sQuery(id+"F3.wireOp",EDGE,"E28"),sQuery(id+"F3.wireOp",EDGE,"E29"),sQuery(id+"F3.wireOp",EDGE,"E30"),sQuery(id+"F3.wireOp",EDGE,"E31"),sQuery(id+"F3.wireOp",EDGE,"E32"),sQuery(id+"F3.wireOp",EDGE,"E33"),sQuery(id+"F3.wireOp",EDGE,"E34"),sQuery(id+"F3.wireOp",EDGE,"E35"),sQuery(id+"F3.wireOp",EDGE,"E36"),sQuery(id+"F3.wireOp",EDGE,"E37"),sQuery(id+"F3.wireOp",EDGE,"E38"),sQuery(id+"F3.wireOp",EDGE,"E39"),sQuery(id+"F3.wireOp",EDGE,"E40"),sQuery(id+"F3.wireOp",EDGE,"E41"),sQuery(id+"F3.wireOp",EDGE,"E42"),sQuery(id+"F3.wireOp",EDGE,"E43"),sQuery(id+"F3.wireOp",EDGE,"E44"),sQuery(id+"F3.wireOp",EDGE,"E45"),sQuery(id+"F3.wireOp",EDGE,"E46"),sQuery(id+"F3.wireOp",EDGE,"E47"),sQuery(id+"F3.wireOp",EDGE,"E48"),sQuery(id+"F3.wireOp",EDGE,"E49"),sQuery(id+"F3.wireOp",EDGE,"E50"),sQuery(id+"F3.wireOp",EDGE,"E51"),sQuery(id+"F3.wireOp",EDGE,"E52"),sQuery(id+"F3.wireOp",EDGE,"E53"),sQuery(id+"F3.wireOp",EDGE,"E54"),sQuery(id+"F3.wireOp",EDGE,"E55"),sQuery(id+"F3.wireOp",EDGE,"E56"),sQuery(id+"F3.wireOp",EDGE,"E57"),sQuery(id+"F3.wireOp",EDGE,"E58"),sQuery(id+"F3.wireOp",EDGE,"E59"),sQuery(id+"F3.wireOp",EDGE,"E60"),sQuery(id+"F3.wireOp",EDGE,"E61"),sQuery(id+"F3.wireOp",EDGE,"E62"),sQuery(id+"F3.wireOp",EDGE,"E63"),sQuery(id+"F3.wireOp",EDGE,"E64"),sQuery(id+"F3.wireOp",EDGE,"E65"),sQuery(id+"F3.wireOp",EDGE,"E66"),sQuery(id+"F3.wireOp",EDGE,"E67"),sQuery(id+"F3.wireOp",EDGE,"E68"),sQuery(id+"F3.wireOp",EDGE,"E69"),sQuery(id+"F3.wireOp",EDGE,"E70"),sQuery(id+"F3.wireOp",EDGE,"E71"),sQuery(id+"F3.wireOp",EDGE,"E72"),sQuery(id+"F3.wireOp",EDGE,"E73")])]});
            var Q4;
            Q4=makeQuery(id+"F1.opRevolve","SWEPT_BODY",BODY,{"disambiguationData":[OSD([sQuery(id+"F0.wireOp",EDGE,"E0"),sQuery(id+"F0.wireOp",EDGE,"E1")])]});
            var Q5;
            Q5=qCreatedBy(makeId("Origin.pointOp"),VERTEX);
            transform(context, id + "F5", {"entities" : qUnion([Q0, Q1, Q2, Q3, Q4]), "transformType" : TransformType.SCALE_UNIFORMLY, "scale" : 0.03, "scalePoint" : qUnion([Q5]), "makeCopy" : false});
        }
        {
            var Q0;
            Q0=qCreatedBy(makeId("Top.planeOp"),FACE);
            var sketch = newSketch(context, id + "F6", { "sketchPlane" : qUnion([Q0])});
            skLineSegment(sketch, "E166", {"start": v(0, 15) * mm, "end": v(0, -15) * mm});
            skArc(sketch, "E167", {"start": v(0, 15) * mm, "mid": v(-15, 0) * mm, "end": v(0, -15) * mm});
            skArc(sketch, "E168", {"start": v(0, 10.25) * mm, "mid": v(-10.25, 0) * mm, "end": v(0, -10.25) * mm});
            skArc(sketch, "E169", {"start": v(0, 7) * mm, "mid": v(-7, 0) * mm, "end": v(0, -7) * mm});
            skSolve(sketch);
        }
        {
            var Q0;
            {var subQ0=sQuery(id+"F6.wireOp",EDGE,"E167");Q0=makeQuery(id+"F6.imprint","IMPRINT",FACE,{"disambiguationData":[TD([[makeQuery(id+"F6.imprint","IMPRINT",EDGE,{"derivedFrom":subQ0}),1.0]])]});}
            var Q1;
            {var subQ0=sQuery(id+"F6.wireOp",EDGE,"E169");Q1=makeQuery(id+"F6.imprint","IMPRINT",FACE,{"disambiguationData":[TD([[makeQuery(id+"F6.imprint","IMPRINT",EDGE,{"derivedFrom":subQ0}),1.0]])]});}
            var Q2;
            Q2=sQuery(id+"F6.wireOp",EDGE,"E166");
            revolve(context, id + "F7", {"operationType" : NewBodyOperationType.REMOVE, "entities" : qUnion([Q0, Q1]), "axis" : qUnion([Q2]), "revolveType" : RevolveType.FULL});
        }
        {
            var Q0;
            Q0=makeQuery(id+"F1.opRevolve","SWEPT_BODY",BODY,{"disambiguationData":[OSD([sQuery(id+"F0.wireOp",EDGE,"E0"),sQuery(id+"F0.wireOp",EDGE,"E1")])]});
            var Q1;
            Q1=sQuery(id+"F0.wireOp",VERTEX,"E1.center");
            transform(context, id + "F8", {"entities" : qUnion([Q0]), "transformType" : TransformType.SCALE_UNIFORMLY, "scale" : 1.4, "scalePoint" : qUnion([Q1]), "makeCopy" : false});
        }
        {
            var Q0;
            Q0=qCreatedBy(makeId("Front.planeOp"),FACE);
            var sketch = newSketch(context, id + "F9", { "sketchPlane" : qUnion([Q0])});
            skCircle(sketch, "E170", {"center": v(0, -5.12) * mm, "radius": 2 * mm});
            skSolve(sketch);
        }
        {
            var Q0;
            Q0=qSketchRegion(id+"F9",true);
            extrude(context, id + "F10", {"entities" : qUnion([Q0]), "operationType" : NewBodyOperationType.REMOVE, "oppositeDirection" : true, "depth" : 25 * mm});
        }
        {
            var Q0;
            Q0=qCreatedBy(makeId("Top.planeOp"),FACE);
            var sketch = newSketch(context, id + "F11", { "sketchPlane" : qUnion([Q0])});
            skLineSegment(sketch, "E171", {"start": v(-31.63, 0) * mm, "end": v(42.46, 0) * mm});
            skSolve(sketch);
        }
        {
            var Q0;
            Q0=sQuery(id+"F11.wireOp",EDGE,"E171");
            cPlane(context, id + "F12", {"entities" : qUnion([Q0]), "cplaneType" : CPlaneType.LINE_ANGLE, "offset" : 25 * mm, "angle" : 40 * degree, "width" : 150 * mm, "height" : 150 * mm});
        }
        {
            var Q0;
            Q0=qCreatedBy(id+"F12.planeOp",FACE);
            var sketch = newSketch(context, id + "F13", { "sketchPlane" : qUnion([Q0])});
            skText(sketch, "E172", { "text": "identity", "fontName": "OpenSans-Italic.ttf"});
            const initialGuessF13  = {"E172": [-0.00938, -0.003, 1, 0, 0.004]};
            skSetInitialGuess(sketch, initialGuessF13);
            skSolve(sketch);
        }
        {
            var Q0;
            Q0=qCreatedBy(makeId("Right.planeOp"),FACE);
            var sketch = newSketch(context, id + "F14", { "sketchPlane" : qUnion([Q0])});
            skArc(sketch, "E173", {"start": v(-4.87, -13.4) * mm, "mid": v(-13.4, 4.87) * mm, "end": v(4.87, 13.4) * mm});
            skLineSegment(sketch, "E174", {"start": v(4.87, 13.4) * mm, "end": v(-4.87, -13.4) * mm});
            skSolve(sketch);
        }
        {
            var Q0;
            Q0=sQuery(id+"F14.wireOp",EDGE,"E173");
            var Q1;
            Q1=sQuery(id+"F14.wireOp",EDGE,"E174");
            revolve(context, id + "F15", {"bodyType" : ToolBodyType.SURFACE, "surfaceEntities" : qUnion([Q0]), "axis" : qUnion([Q1]), "revolveType" : RevolveType.FULL});
        }
        {
            var Q0;
            Q0 = qSketchRegion(id + "F13", true);
            var Q1;
            Q1=makeQuery(id+"F15.opRevolve","SWEPT_FACE",FACE,{"disambiguationData":[OSD([sQuery(id+"F14.wireOp",EDGE,"E173")])]});
            extrude(context, id + "F16", {"entities" : qUnion([Q0]), "operationType" : NewBodyOperationType.ADD, "endBound" : BoundingType.UP_TO_SURFACE, "depth" : 25 * mm, "endBoundEntityFace" : qUnion([Q1]), "offsetDistance" : 25 * mm});
        }
    });
